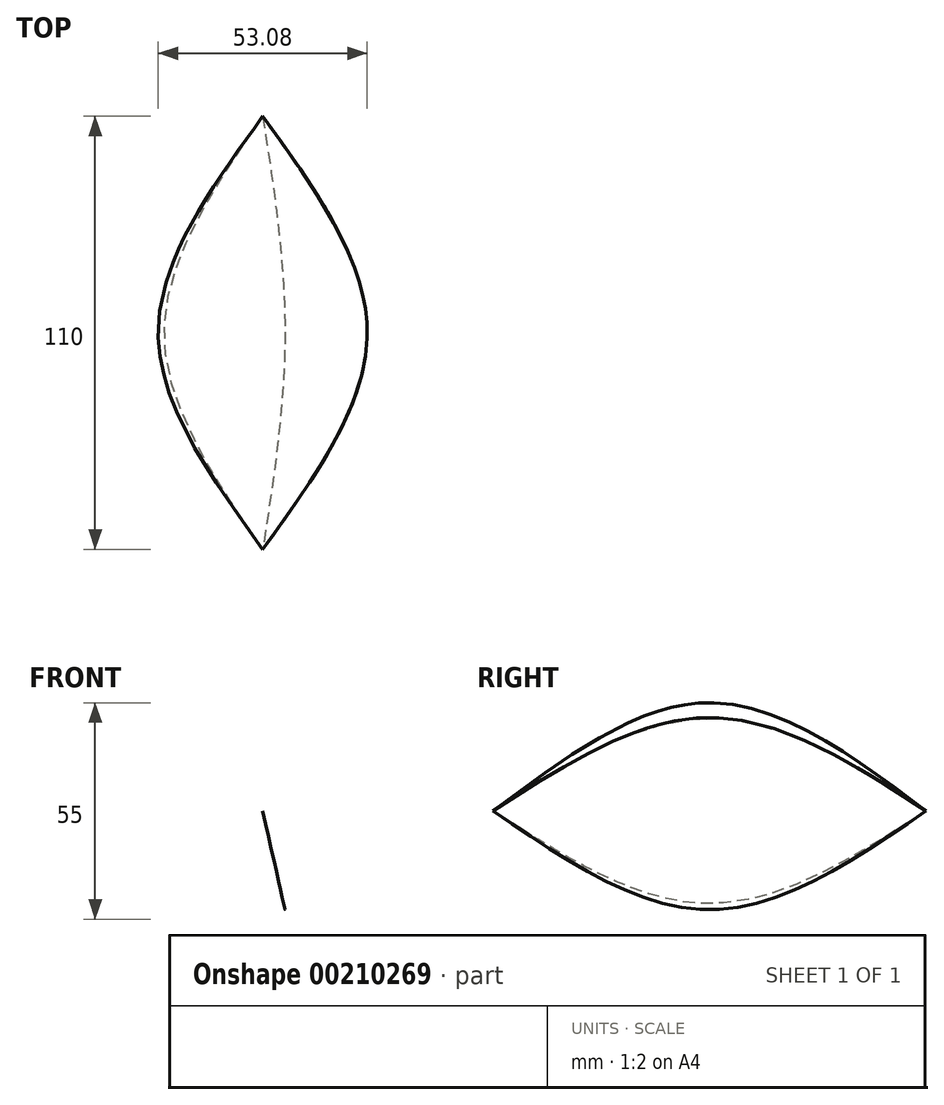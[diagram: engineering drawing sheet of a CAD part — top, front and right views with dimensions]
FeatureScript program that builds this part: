
annotation { "Feature Type Name" : "Feature", "Feature Type Description" : "" }
export const myFeature = defineFeature(function(context is Context, id is Id, definition is map)
    precondition{}
    {
        {
            var Q0;
            Q0=qCreatedBy(makeId("Front.planeOp"),FACE);
            var sketch = newSketch(context, id + "F0", { "sketchPlane" : qUnion([Q0])});
            skCircle(sketch, "E0", {"center": v(0, 0) * mm, "radius": 27.5 * mm});
            skCircle(sketch, "E1.cCircle", {"center": v(0, 0) * mm, "radius": 22.5 * mm, "construction": true});
            skLineSegment(sketch, "E1.0", {"start": v(-7.31, 22.5) * mm, "end": v(7.31, 22.5) * mm});
            skLineSegment(sketch, "E1.1", {"start": v(7.31, 22.5) * mm, "end": v(19.14, 13.9) * mm});
            skLineSegment(sketch, "E1.2", {"start": v(19.14, 13.9) * mm, "end": v(23.66, 0) * mm});
            skLineSegment(sketch, "E1.3", {"start": v(23.66, 0) * mm, "end": v(19.14, -13.9) * mm});
            skLineSegment(sketch, "E1.4", {"start": v(19.14, -13.9) * mm, "end": v(7.31, -22.5) * mm});
            skLineSegment(sketch, "E1.5", {"start": v(7.31, -22.5) * mm, "end": v(-7.31, -22.5) * mm});
            skLineSegment(sketch, "E1.6", {"start": v(-7.31, -22.5) * mm, "end": v(-19.14, -13.9) * mm});
            skLineSegment(sketch, "E1.7", {"start": v(-19.14, -13.9) * mm, "end": v(-23.66, 0) * mm});
            skLineSegment(sketch, "E1.8", {"start": v(-23.66, 0) * mm, "end": v(-19.14, 13.9) * mm});
            skLineSegment(sketch, "E1.9", {"start": v(-19.14, 13.9) * mm, "end": v(-7.31, 22.5) * mm});
            skPoint(sketch, "E1.0.midPoint", {"position": v(0, 22.5) * mm});
            skSolve(sketch);
        }
        {
            var Q0;
            Q0=qCreatedBy(makeId("Front.planeOp"),FACE);
            var sketch = newSketch(context, id + "F1", { "sketchPlane" : qUnion([Q0])});
            skArc(sketch, "E2", {"start": v(5.66, 25.08) * mm, "mid": v(0, 27.5) * mm, "end": v(-5.66, 25.08) * mm});
            skArc(sketch, "E3.1.0", {"start": v(-10.16, 23.62) * mm, "mid": v(-16.16, 22.25) * mm, "end": v(-19.33, 16.96) * mm});
            skArc(sketch, "E3.2.0", {"start": v(-22.1, 13.14) * mm, "mid": v(-26.15, 8.5) * mm, "end": v(-25.6, 2.36) * mm});
            skArc(sketch, "E3.3.0", {"start": v(-25.6, -2.36) * mm, "mid": v(-26.15, -8.5) * mm, "end": v(-22.1, -13.14) * mm});
            skArc(sketch, "E3.4.0", {"start": v(-19.33, -16.96) * mm, "mid": v(-16.16, -22.25) * mm, "end": v(-10.16, -23.62) * mm});
            skArc(sketch, "E3.5.0", {"start": v(-5.66, -25.08) * mm, "mid": v(0, -27.5) * mm, "end": v(5.66, -25.08) * mm});
            skArc(sketch, "E3.6.0", {"start": v(10.16, -23.62) * mm, "mid": v(16.16, -22.25) * mm, "end": v(19.33, -16.96) * mm});
            skArc(sketch, "E3.7.0", {"start": v(22.1, -13.14) * mm, "mid": v(26.15, -8.5) * mm, "end": v(25.6, -2.36) * mm});
            skArc(sketch, "E3.8.0", {"start": v(25.6, 2.36) * mm, "mid": v(26.15, 8.5) * mm, "end": v(22.1, 13.14) * mm});
            skArc(sketch, "E3.9.0", {"start": v(19.33, 16.96) * mm, "mid": v(16.16, 22.25) * mm, "end": v(10.16, 23.62) * mm});
            skPoint(sketch, "E3.center", {"position": v(0, 0) * mm});
            skPoint(sketch, "E4.visualSharp", {"position": v(-7.31, 22.5) * mm});
            skArc(sketch, "E4.filletArc", {"start": v(-10.16, 23.62) * mm, "mid": v(-7.73, 23.79) * mm, "end": v(-5.66, 25.08) * mm});
            skPoint(sketch, "E5.visualSharp", {"position": v(7.31, 22.5) * mm});
            skArc(sketch, "E5.filletArc", {"start": v(5.66, 25.08) * mm, "mid": v(7.73, 23.79) * mm, "end": v(10.16, 23.62) * mm});
            skPoint(sketch, "E6.visualSharp", {"position": v(19.14, 13.9) * mm});
            skArc(sketch, "E6.filletArc", {"start": v(19.33, 16.96) * mm, "mid": v(20.23, 14.7) * mm, "end": v(22.1, 13.14) * mm});
            skPoint(sketch, "E7.visualSharp", {"position": v(23.66, 0) * mm});
            skArc(sketch, "E7.filletArc", {"start": v(25.6, 2.36) * mm, "mid": v(25.01, 0) * mm, "end": v(25.6, -2.36) * mm});
            skPoint(sketch, "E8.visualSharp", {"position": v(19.14, -13.9) * mm});
            skArc(sketch, "E8.filletArc", {"start": v(22.1, -13.14) * mm, "mid": v(20.23, -14.7) * mm, "end": v(19.33, -16.96) * mm});
            skPoint(sketch, "E9.visualSharp", {"position": v(7.31, -22.5) * mm});
            skArc(sketch, "E9.filletArc", {"start": v(10.16, -23.62) * mm, "mid": v(7.73, -23.79) * mm, "end": v(5.66, -25.08) * mm});
            skPoint(sketch, "E10.visualSharp", {"position": v(-7.31, -22.5) * mm});
            skArc(sketch, "E10.filletArc", {"start": v(-5.66, -25.08) * mm, "mid": v(-7.73, -23.79) * mm, "end": v(-10.16, -23.62) * mm});
            skPoint(sketch, "E11.visualSharp", {"position": v(-19.14, -13.9) * mm});
            skArc(sketch, "E11.filletArc", {"start": v(-19.33, -16.96) * mm, "mid": v(-20.23, -14.7) * mm, "end": v(-22.1, -13.14) * mm});
            skPoint(sketch, "E12.visualSharp", {"position": v(-23.66, 0) * mm});
            skArc(sketch, "E12.filletArc", {"start": v(-25.6, -2.36) * mm, "mid": v(-25.01, 0) * mm, "end": v(-25.6, 2.36) * mm});
            skPoint(sketch, "E13.visualSharp", {"position": v(-19.14, 13.9) * mm});
            skArc(sketch, "E13.filletArc", {"start": v(-22.1, 13.14) * mm, "mid": v(-20.23, 14.7) * mm, "end": v(-19.33, 16.96) * mm});
            skSolve(sketch);
        }
        {
            var Q0;
            Q0=qCreatedBy(makeId("Right.planeOp"),FACE);
            var sketch = newSketch(context, id + "F2", { "sketchPlane" : qUnion([Q0])});
            skLineSegment(sketch, "E14", {"start": v(55, 0) * mm, "end": v(0, 0) * mm, "construction": true});
            skLineSegment(sketch, "E15", {"start": v(0, 0) * mm, "end": v(-55, 0) * mm, "construction": true});
            skPoint(sketch, "E16", {"position": v(55, 0) * mm});
            skPoint(sketch, "E17", {"position": v(-55, 0) * mm});
            skSolve(sketch);
        }
        {
            var Q0;
            Q0=sQuery(id+"F2.wireOp",VERTEX,"E16");
            var Q1;
            Q1 = qSketchRegion(id + "F1", true);
            var Q2;
            Q2=sQuery(id+"F2.wireOp",VERTEX,"E17");
            loft(context, id + "F3", {"sheetProfilesArray" : [{ "sheetProfileEntities" : qUnion([Q0]) }, { "sheetProfileEntities" : qUnion([Q1]) }, { "sheetProfileEntities" : qUnion([Q2]) }]});
        }
    });
